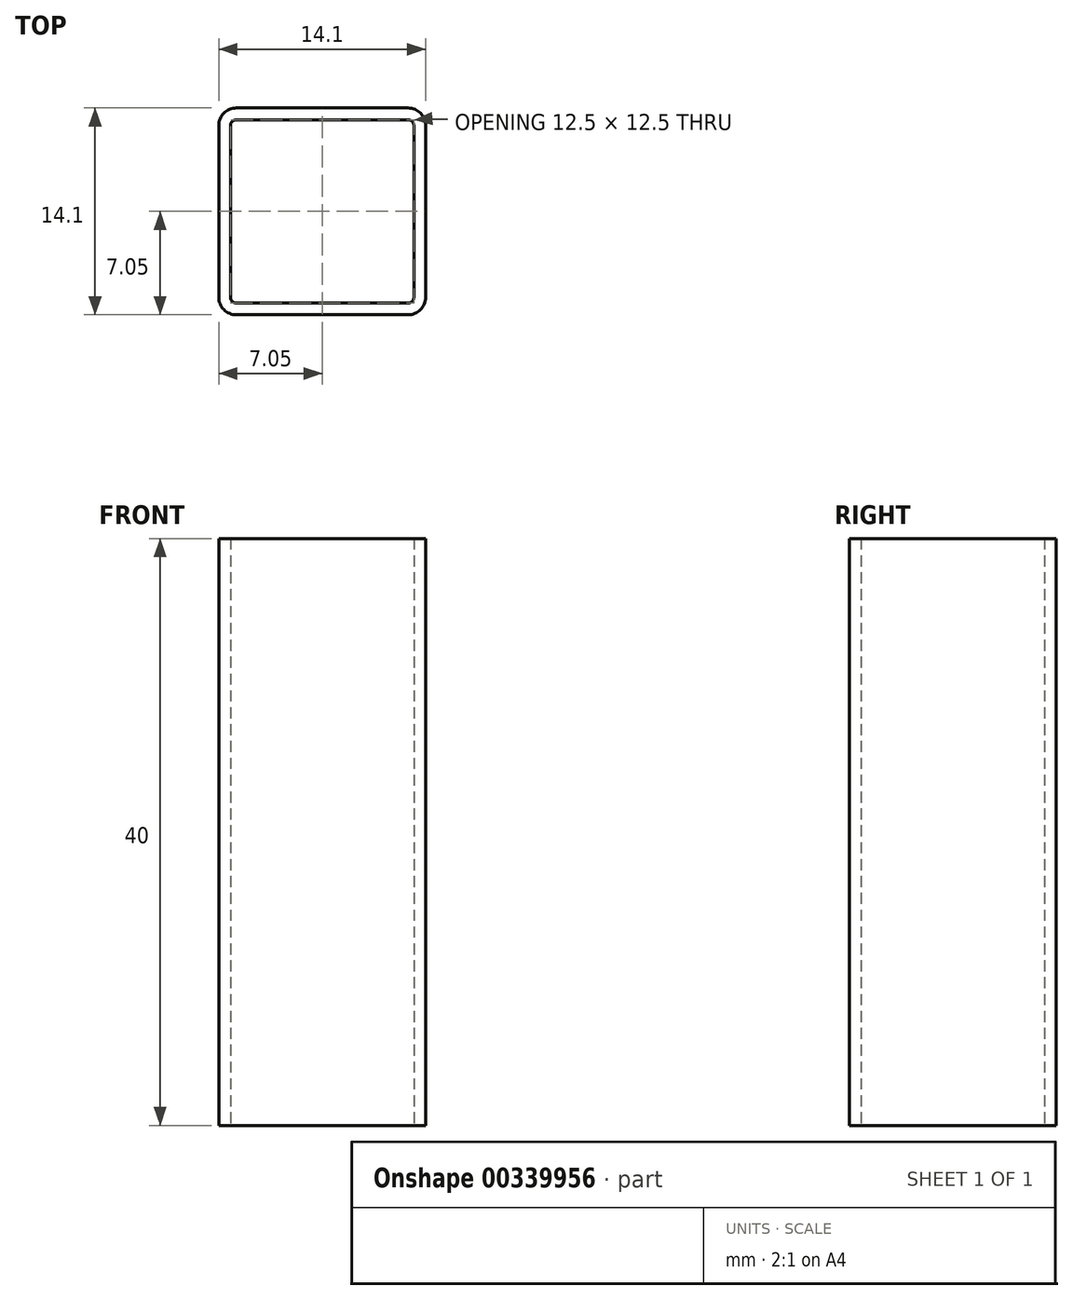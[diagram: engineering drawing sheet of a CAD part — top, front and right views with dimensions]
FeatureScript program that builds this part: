
annotation { "Feature Type Name" : "Feature", "Feature Type Description" : "" }
export const myFeature = defineFeature(function(context is Context, id is Id, definition is map)
    precondition{}
    {
        {
            var Q0;
            Q0=qCreatedBy(makeId("Top.planeOp"),FACE);
            var sketch = newSketch(context, id + "F0", { "sketchPlane" : qUnion([Q0])});
            skLineSegment(sketch, "E0.bottom", {"start": v(6.25, -6.25) * mm, "end": v(-6.25, -6.25) * mm});
            skLineSegment(sketch, "E0.top", {"start": v(6.25, 6.25) * mm, "end": v(-6.25, 6.25) * mm});
            skLineSegment(sketch, "E0.left", {"start": v(6.25, -6.25) * mm, "end": v(6.25, 6.25) * mm});
            skLineSegment(sketch, "E0.right", {"start": v(-6.25, -6.25) * mm, "end": v(-6.25, 6.25) * mm});
            skPoint(sketch, "E0.middle", {"position": v(0, 0) * mm});
            skLineSegment(sketch, "E1.bottom", {"start": v(-7.05, 7.05) * mm, "end": v(7.05, 7.05) * mm});
            skLineSegment(sketch, "E1.top", {"start": v(-7.05, -7.05) * mm, "end": v(7.05, -7.05) * mm});
            skLineSegment(sketch, "E1.left", {"start": v(-7.05, 7.05) * mm, "end": v(-7.05, -7.05) * mm});
            skLineSegment(sketch, "E1.right", {"start": v(7.05, 7.05) * mm, "end": v(7.05, -7.05) * mm});
            skSolve(sketch);
        }
        {
            var Q0;
            Q0=qSketchRegion(id+"F0",true);
            extrude(context, id + "F1", {"entities" : qUnion([Q0]), "depth" : 40 * mm});
        }
        {
            var Q0;
            Q0=makeQuery(id+"F1.opExtrude","SWEPT_EDGE",EDGE,{"disambiguationData":[OSD([sQuery(id+"F0.wireOp",EDGE,"E0.bottom"),sQuery(id+"F0.wireOp",EDGE,"E0.right")])]});
            var Q1;
            Q1=makeQuery(id+"F1.opExtrude","SWEPT_EDGE",EDGE,{"disambiguationData":[OSD([sQuery(id+"F0.wireOp",EDGE,"E0.top"),sQuery(id+"F0.wireOp",EDGE,"E0.left")])]});
            var Q2;
            Q2=makeQuery(id+"F1.opExtrude","SWEPT_EDGE",EDGE,{"disambiguationData":[OSD([sQuery(id+"F0.wireOp",EDGE,"E0.bottom"),sQuery(id+"F0.wireOp",EDGE,"E0.left")])]});
            var Q3;
            Q3=makeQuery(id+"F1.opExtrude","SWEPT_EDGE",EDGE,{"disambiguationData":[OSD([sQuery(id+"F0.wireOp",EDGE,"E0.top"),sQuery(id+"F0.wireOp",EDGE,"E0.right")])]});
            fillet(context, id + "F2", {"entities" : qUnion([Q0, Q1, Q2, Q3]), "radius" : 0.4 * mm, "tangentPropagation" : true, "allowEdgeOverflow" : false});
        }
        {
            var Q0;
            Q0=makeQuery(id+"F1.opExtrude","SWEPT_EDGE",EDGE,{"disambiguationData":[OSD([sQuery(id+"F0.wireOp",EDGE,"E1.top"),sQuery(id+"F0.wireOp",EDGE,"E1.right")])]});
            var Q1;
            Q1=makeQuery(id+"F1.opExtrude","SWEPT_EDGE",EDGE,{"disambiguationData":[OSD([sQuery(id+"F0.wireOp",EDGE,"E1.bottom"),sQuery(id+"F0.wireOp",EDGE,"E1.right")])]});
            var Q2;
            Q2=makeQuery(id+"F1.opExtrude","SWEPT_EDGE",EDGE,{"disambiguationData":[OSD([sQuery(id+"F0.wireOp",EDGE,"E1.top"),sQuery(id+"F0.wireOp",EDGE,"E1.left")])]});
            var Q3;
            Q3=makeQuery(id+"F1.opExtrude","SWEPT_EDGE",EDGE,{"disambiguationData":[OSD([sQuery(id+"F0.wireOp",EDGE,"E1.bottom"),sQuery(id+"F0.wireOp",EDGE,"E1.left")])]});
            fillet(context, id + "F3", {"entities" : qUnion([Q0, Q1, Q2, Q3]), "radius" : 1.2 * mm, "tangentPropagation" : true, "allowEdgeOverflow" : false});
        }
    });
